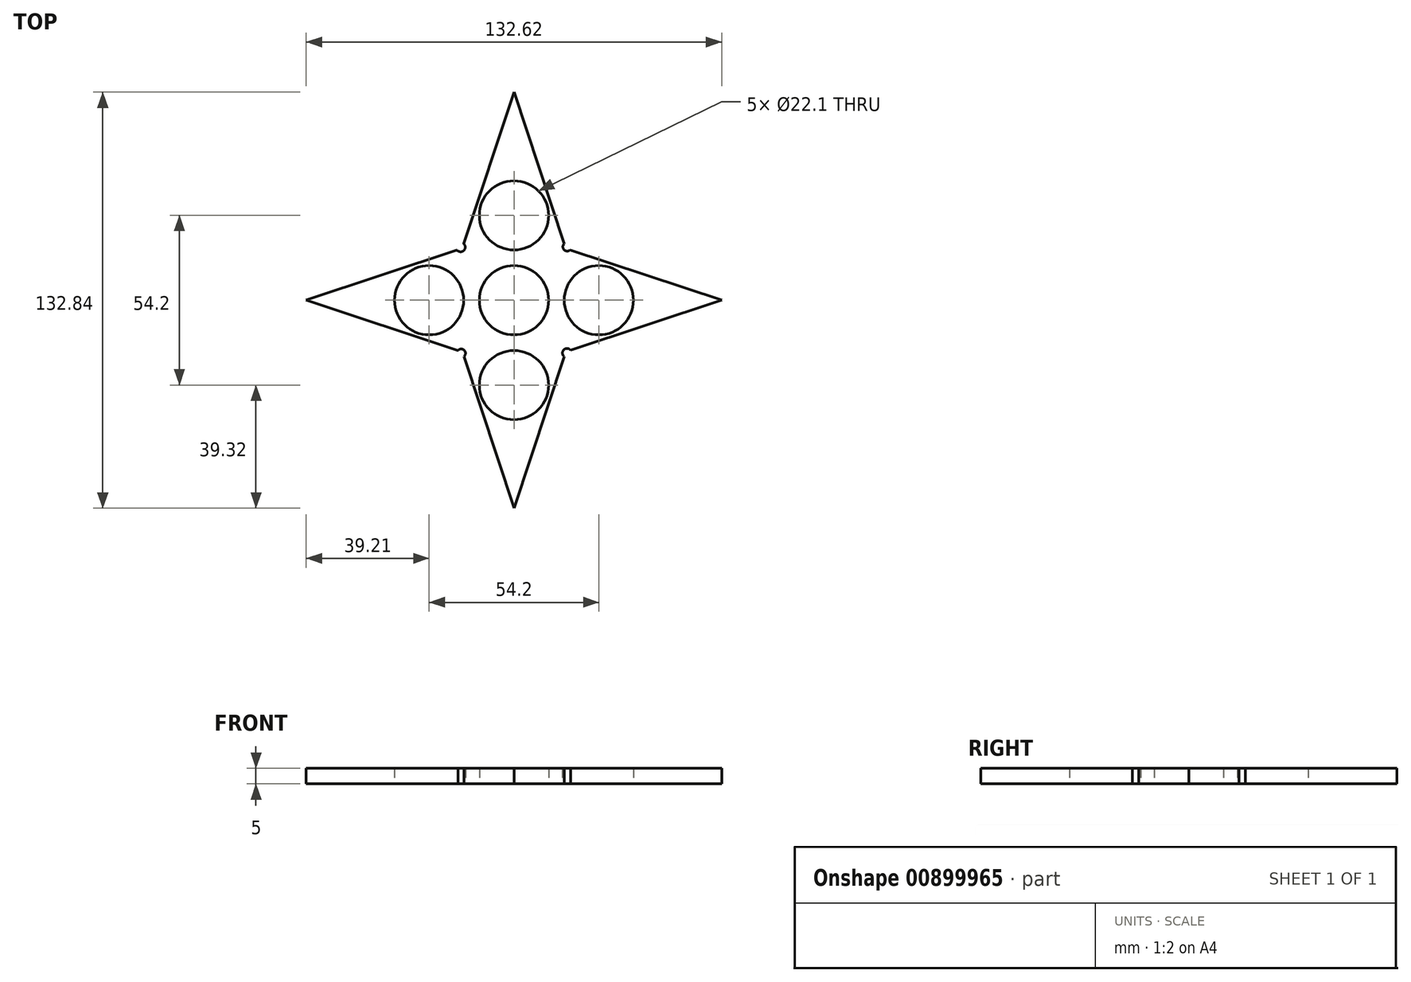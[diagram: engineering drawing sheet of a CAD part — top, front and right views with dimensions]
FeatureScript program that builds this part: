
annotation { "Feature Type Name" : "Feature", "Feature Type Description" : "" }
export const myFeature = defineFeature(function(context is Context, id is Id, definition is map)
    precondition{}
    {
        {
            var Q0;
            Q0=qCreatedBy(makeId("Top.planeOp"),FACE);
            var sketch = newSketch(context, id + "F0", { "sketchPlane" : qUnion([Q0])});
            skPoint(sketch, "E0", {"position": v(0, 0) * mm});
            skLineSegment(sketch, "E1", {"start": v(0, 18) * mm, "end": v(-16.02, 18) * mm});
            skLineSegment(sketch, "E2", {"start": v(-16.02, 18) * mm, "end": v(0, 66.42) * mm});
            skLineSegment(sketch, "E3", {"start": v(0, 66.42) * mm, "end": v(0, 18) * mm});
            skLineSegment(sketch, "E4", {"start": v(16, 18) * mm, "end": v(0, 66.42) * mm});
            skLineSegment(sketch, "E5", {"start": v(16, 18) * mm, "end": v(0, 18) * mm});
            skLineSegment(sketch, "E6", {"start": v(18, 0) * mm, "end": v(17.87, 16.02) * mm});
            skLineSegment(sketch, "E7", {"start": v(17.87, 16.02) * mm, "end": v(66.3, 0) * mm});
            skLineSegment(sketch, "E8", {"start": v(66.3, 0) * mm, "end": v(18, 0) * mm});
            skLineSegment(sketch, "E9", {"start": v(18.13, -16) * mm, "end": v(66.3, 0) * mm});
            skLineSegment(sketch, "E10", {"start": v(18.13, -16) * mm, "end": v(18, 0) * mm});
            skLineSegment(sketch, "E11.0", {"start": v(18, 0) * mm, "end": v(18.13, -16) * mm, "construction": true});
            skLineSegment(sketch, "E12", {"start": v(0, -18) * mm, "end": v(16.02, -18) * mm});
            skLineSegment(sketch, "E13", {"start": v(16.02, -18) * mm, "end": v(0, -66.42) * mm});
            skLineSegment(sketch, "E14", {"start": v(0, -66.42) * mm, "end": v(0, -18) * mm});
            skLineSegment(sketch, "E15", {"start": v(-16, -18) * mm, "end": v(0, -66.42) * mm});
            skLineSegment(sketch, "E16", {"start": v(-16, -18) * mm, "end": v(0, -18) * mm});
            skLineSegment(sketch, "E17", {"start": v(-18, 0) * mm, "end": v(-17.87, -16.02) * mm});
            skLineSegment(sketch, "E18", {"start": v(-17.87, -16.02) * mm, "end": v(-66.3, 0) * mm});
            skLineSegment(sketch, "E19", {"start": v(-66.3, 0) * mm, "end": v(-18, 0) * mm});
            skLineSegment(sketch, "E20", {"start": v(-18.13, 16) * mm, "end": v(-66.3, 0) * mm});
            skLineSegment(sketch, "E21", {"start": v(-18.13, 16) * mm, "end": v(-18, 0) * mm});
            skLineSegment(sketch, "E22.0", {"start": v(-18, 0) * mm, "end": v(-18.13, 16) * mm, "construction": true});
            skArc(sketch, "E23", {"start": v(-18.13, 16) * mm, "mid": v(-16, 15.87) * mm, "end": v(-16.02, 18) * mm});
            skArc(sketch, "E24", {"start": v(16, 18) * mm, "mid": v(15.97, 16.1) * mm, "end": v(17.87, 16.02) * mm});
            skArc(sketch, "E25", {"start": v(-16, -18) * mm, "mid": v(-15.86, -16) * mm, "end": v(-17.87, -16.02) * mm});
            skArc(sketch, "E26", {"start": v(18.13, -16) * mm, "mid": v(15.94, -15.8) * mm, "end": v(16.02, -18) * mm});
            skSolve(sketch);
        }
        {
            var Q0;
            Q0=makeQuery(id+"F0.imprint","IMPRINT",FACE,{"disambiguationData":[TD([[makeQuery(id+"F0.imprint","IMPRINT",EDGE,{"derivedFrom":sQuery(id+"F0.wireOp",EDGE,"E1")}),-1.0]])]});
            var Q1;
            Q1=makeQuery(id+"F0.imprint","IMPRINT",FACE,{"disambiguationData":[TD([[makeQuery(id+"F0.imprint","IMPRINT",EDGE,{"derivedFrom":sQuery(id+"F0.wireOp",EDGE,"E3")}),1.0]])]});
            var Q2;
            Q2=makeQuery(id+"F0.imprint","IMPRINT",FACE,{"disambiguationData":[TD([[makeQuery(id+"F0.imprint","IMPRINT",EDGE,{"derivedFrom":sQuery(id+"F0.wireOp",EDGE,"E12")}),-1.0]])]});
            var Q3;
            Q3=makeQuery(id+"F0.imprint","IMPRINT",FACE,{"disambiguationData":[TD([[makeQuery(id+"F0.imprint","IMPRINT",EDGE,{"derivedFrom":sQuery(id+"F0.wireOp",EDGE,"E1")}),1.0]])]});
            var Q4;
            Q4=makeQuery(id+"F0.imprint","IMPRINT",FACE,{"disambiguationData":[TD([[makeQuery(id+"F0.imprint","IMPRINT",EDGE,{"derivedFrom":sQuery(id+"F0.wireOp",EDGE,"E6")}),-1.0]])]});
            var Q5;
            Q5=makeQuery(id+"F0.imprint","IMPRINT",FACE,{"disambiguationData":[TD([[makeQuery(id+"F0.imprint","IMPRINT",EDGE,{"derivedFrom":sQuery(id+"F0.wireOp",EDGE,"E8")}),1.0]])]});
            var Q6;
            Q6=makeQuery(id+"F0.imprint","IMPRINT",FACE,{"disambiguationData":[TD([[makeQuery(id+"F0.imprint","IMPRINT",EDGE,{"derivedFrom":sQuery(id+"F0.wireOp",EDGE,"E14")}),1.0]])]});
            var Q7;
            Q7=makeQuery(id+"F0.imprint","IMPRINT",FACE,{"disambiguationData":[TD([[makeQuery(id+"F0.imprint","IMPRINT",EDGE,{"derivedFrom":sQuery(id+"F0.wireOp",EDGE,"E17")}),-1.0]])]});
            var Q8;
            Q8=makeQuery(id+"F0.imprint","IMPRINT",FACE,{"disambiguationData":[TD([[makeQuery(id+"F0.imprint","IMPRINT",EDGE,{"derivedFrom":sQuery(id+"F0.wireOp",EDGE,"E19")}),1.0]])]});
            extrude(context, id + "F1", {"entities" : qUnion([Q0, Q1, Q2, Q3, Q4, Q5, Q6, Q7, Q8]), "depth" : 5 * mm, "offsetDistance" : 25 * mm});
        }
        {
            var Q0;
            Q0=qCreatedBy(makeId("Top.planeOp"),FACE);
            var sketch = newSketch(context, id + "F2", { "sketchPlane" : qUnion([Q0])});
            skCircle(sketch, "E27", {"center": v(0, 0) * mm, "radius": 11.05 * mm});
            skCircle(sketch, "E28", {"center": v(0, 27.1) * mm, "radius": 11.05 * mm});
            skCircle(sketch, "E29", {"center": v(27.1, 0) * mm, "radius": 11.05 * mm});
            skCircle(sketch, "E30", {"center": v(-27.1, 0) * mm, "radius": 11.05 * mm});
            skCircle(sketch, "E31", {"center": v(0, -27.1) * mm, "radius": 11.05 * mm});
            skSolve(sketch);
        }
        {
            var Q0;
            Q0=makeQuery(id+"F2.imprint","IMPRINT",FACE,{"disambiguationData":[TD([[makeQuery(id+"F2.imprint","IMPRINT",EDGE,{"derivedFrom":sQuery(id+"F2.wireOp",EDGE,"E28")}),1.0]])]});
            var Q1;
            Q1=makeQuery(id+"F2.imprint","IMPRINT",FACE,{"disambiguationData":[TD([[makeQuery(id+"F2.imprint","IMPRINT",EDGE,{"derivedFrom":sQuery(id+"F2.wireOp",EDGE,"E27")}),1.0]])]});
            var Q2;
            Q2=makeQuery(id+"F2.imprint","IMPRINT",FACE,{"disambiguationData":[TD([[makeQuery(id+"F2.imprint","IMPRINT",EDGE,{"derivedFrom":sQuery(id+"F2.wireOp",EDGE,"E30")}),1.0]])]});
            var Q3;
            Q3=makeQuery(id+"F2.imprint","IMPRINT",FACE,{"disambiguationData":[TD([[makeQuery(id+"F2.imprint","IMPRINT",EDGE,{"derivedFrom":sQuery(id+"F2.wireOp",EDGE,"E29")}),1.0]])]});
            var Q4;
            Q4=makeQuery(id+"F2.imprint","IMPRINT",FACE,{"disambiguationData":[TD([[makeQuery(id+"F2.imprint","IMPRINT",EDGE,{"derivedFrom":sQuery(id+"F2.wireOp",EDGE,"E31")}),1.0]])]});
            extrude(context, id + "F3", {"entities" : qUnion([Q0, Q1, Q2, Q3, Q4]), "operationType" : NewBodyOperationType.REMOVE, "depth" : 21.4 * mm, "offsetDistance" : 25 * mm});
        }
    });
